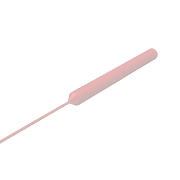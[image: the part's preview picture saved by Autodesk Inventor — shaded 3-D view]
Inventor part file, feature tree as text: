
AUTODESK INVENTOR PART (.ipt)
format: ipt  version: 2019 (Build 230136000, 136)  size: 92,672 bytes
history: native  units: mm
features: sketch x3, extrude x3, plane x2, other x2, reference x1, projected_geometry x1
ambient origin geometry x8: Origin, YZ Plane, XZ Plane, XY Plane, X Axis, Y Axis, Z Axis, Center Point
bodies: Solid1 (feature_tree)
feature tree (12):
  sketch  "Sketch1"  dims[d0=4.0mm d1=10.0mm d2=0.0mm]
  plane  "Work Plane1"
  extrude  "Extrusion1"  Depth=10.0mm TaperAngle=0.0deg
  extrude  "Extrusion2"  Depth=2.0mm TaperAngle=0.0deg
  sketch  "Sketch3"
  plane  "Work Plane2"
  extrude  "Extrusion3"  [1 undecoded]
  reference  "Reference1"
  sketch  "Sketch2"  dims[d3=2.0mm d4=-6.981317mm d5=2.0mm d6=0.0mm]
  projected_geometry  "Projected Loop1"
  other  "cellSTORM_v3_flexure.iam"
  other  "00_LASER_640nm:1"
note: 1 required parameter value undecoded (feature->parameter linkage not recoverable at this tier; creation-order binding heuristic only, values carry confidence <= 0.55)
